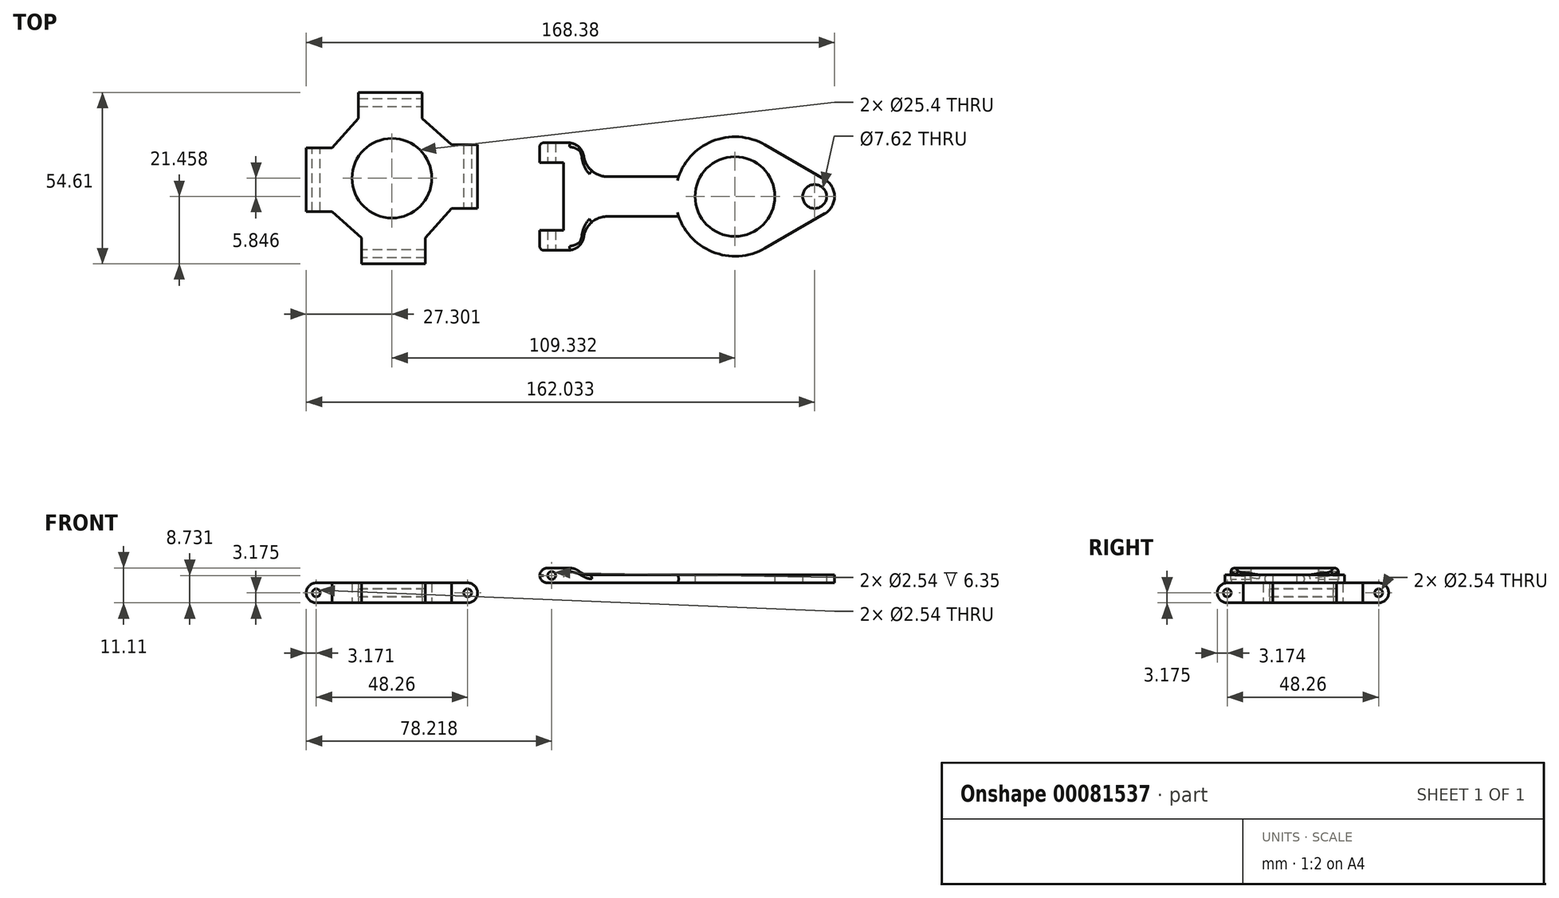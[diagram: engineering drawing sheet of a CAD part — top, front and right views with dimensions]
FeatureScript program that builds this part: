
annotation { "Feature Type Name" : "Feature", "Feature Type Description" : "" }
export const myFeature = defineFeature(function(context is Context, id is Id, definition is map)
    precondition{}
    {
        {
            var Q0;
            Q0=qCreatedBy(makeId("Top.planeOp"),FACE);
            var sketch = newSketch(context, id + "F0", { "sketchPlane" : qUnion([Q0])});
            skLineSegment(sketch, "E0.bottom", {"start": v(2.73, 19.55) * mm, "end": v(-35.37, 19.55) * mm});
            skLineSegment(sketch, "E0.top", {"start": v(2.73, -18.55) * mm, "end": v(-35.37, -18.55) * mm});
            skLineSegment(sketch, "E0.left", {"start": v(2.73, 19.55) * mm, "end": v(2.73, -18.55) * mm});
            skLineSegment(sketch, "E0.right", {"start": v(-35.37, 19.55) * mm, "end": v(-35.37, -18.55) * mm});
            skPoint(sketch, "E0.middle", {"position": v(-16.32, 0.5) * mm});
            skCircle(sketch, "E1", {"center": v(-16.32, 0.5) * mm, "radius": 12.7 * mm});
            skSolve(sketch);
        }
        {
            var Q0;
            Q0 = qSketchRegion(id + "F0", true);
            extrude(context, id + "F1", {"entities" : qUnion([Q0]), "depth" : 6.35 * mm});
        }
        {
            var Q0;
            Q0=qCreatedBy(makeId("Front.planeOp"),FACE);
            var sketch = newSketch(context, id + "F2", { "sketchPlane" : qUnion([Q0])});
            skCircle(sketch, "E2", {"center": v(-40.45, 3.17) * mm, "radius": 3.18 * mm});
            skCircle(sketch, "E3", {"center": v(-40.45, 3.17) * mm, "radius": 1.27 * mm});
            skLineSegment(sketch, "E4", {"start": v(-40.45, 6.35) * mm, "end": v(-35.37, 6.35) * mm});
            skLineSegment(sketch, "E5", {"start": v(-35.37, 6.35) * mm, "end": v(-35.37, 0) * mm});
            skLineSegment(sketch, "E6", {"start": v(-35.37, 0) * mm, "end": v(-40.45, 0) * mm});
            skSolve(sketch);
        }
        {
            var Q0;
            Q0 = qSketchRegion(id + "F2", true);
            extrude(context, id + "F3", {"entities" : qUnion([Q0]), "operationType" : NewBodyOperationType.ADD, "depth" : 10.16 * mm, "hasSecondDirection" : true, "secondDirectionOppositeDirection" : true, "secondDirectionDepth" : 10.16 * mm});
        }
        {
            var Q0;
            Q0=makeQuery(id+"F1.opExtrude","SWEPT_BODY",BODY,{"disambiguationData":[OSD([sQuery(id+"F0.wireOp",EDGE,"E0.bottom"),sQuery(id+"F0.wireOp",EDGE,"E0.top"),sQuery(id+"F0.wireOp",EDGE,"E0.left"),sQuery(id+"F0.wireOp",EDGE,"E0.right"),sQuery(id+"F0.wireOp",EDGE,"E1")])]});
            var Q1;
            Q1=makeQuery(id+"F1.opExtrude","CAP_EDGE",EDGE,{"disambiguationData":[OSD([sQuery(id+"F0.wireOp",EDGE,"E1")])],"isStart":false});
            circularPattern(context, id + "F4", {"operationType" : NewBodyOperationType.ADD, "entities" : qUnion([Q0]), "axis" : qUnion([Q1]), "angle" : 90 * degree, "instanceCount" : 4});
        }
        {
            var Q0;
            {var subQ0=makeQuery(id+"F3.boolean.opBoolean","MERGE",FACE,{"derivedFrom":[makeQuery(id+"F1.opExtrude","CAP_FACE",FACE,{"disambiguationData":[OSD([sQuery(id+"F0.wireOp",EDGE,"E0.bottom"),sQuery(id+"F0.wireOp",EDGE,"E0.top"),sQuery(id+"F0.wireOp",EDGE,"E0.left"),sQuery(id+"F0.wireOp",EDGE,"E0.right"),sQuery(id+"F0.wireOp",EDGE,"E1")])],"isStart":false}),makeQuery(id+"F3.opExtrude","SWEPT_FACE",FACE,{"disambiguationData":[OSD([sQuery(id+"F2.wireOp",EDGE,"E4")])]})]});Q0=makeQuery(id+"F4.boolean.opBoolean","MERGE",FACE,{"derivedFrom":[subQ0,makeQuery(id+"F4.opPattern","COPY",FACE,{"derivedFrom":subQ0,"instanceName":"1"}),makeQuery(id+"F4.opPattern","COPY",FACE,{"derivedFrom":subQ0,"instanceName":"2"}),makeQuery(id+"F4.opPattern","COPY",FACE,{"derivedFrom":subQ0,"instanceName":"3"})]});}
            var sketch = newSketch(context, id + "F5", { "sketchPlane" : qUnion([Q0])});
            skLineSegment(sketch, "E7", {"start": v(-26.98, 19.55) * mm, "end": v(-35.37, 10.16) * mm});
            skLineSegment(sketch, "E8", {"start": v(-35.37, 10.16) * mm, "end": v(-40.75, 19.55) * mm});
            skLineSegment(sketch, "E9", {"start": v(-40.75, 19.55) * mm, "end": v(-26.98, 19.55) * mm});
            skLineSegment(sketch, "E10", {"start": v(-6.66, 19.55) * mm, "end": v(2.73, 11.17) * mm});
            skLineSegment(sketch, "E11", {"start": v(2.73, 11.17) * mm, "end": v(6.16, 21.92) * mm});
            skLineSegment(sketch, "E12", {"start": v(6.16, 21.92) * mm, "end": v(-6.66, 19.55) * mm});
            skLineSegment(sketch, "E13", {"start": v(-35.37, -10.16) * mm, "end": v(-25.98, -18.55) * mm});
            skLineSegment(sketch, "E14", {"start": v(-25.98, -18.55) * mm, "end": v(-39.65, -26.32) * mm});
            skLineSegment(sketch, "E15", {"start": v(-39.65, -26.32) * mm, "end": v(-35.37, -10.16) * mm});
            skLineSegment(sketch, "E16", {"start": v(-5.66, -18.55) * mm, "end": v(10.18, -22.29) * mm});
            skLineSegment(sketch, "E17", {"start": v(10.18, -22.29) * mm, "end": v(2.73, -9.15) * mm});
            skLineSegment(sketch, "E18", {"start": v(2.73, -9.15) * mm, "end": v(-5.66, -18.55) * mm});
            skSolve(sketch);
        }
        {
            var Q0;
            Q0 = qSketchRegion(id + "F5", true);
            extrude(context, id + "F6", {"entities" : qUnion([Q0]), "operationType" : NewBodyOperationType.REMOVE, "endBound" : BoundingType.THROUGH_ALL, "oppositeDirection" : true, "depth" : 25.4 * mm});
        }
        {
            var Q0;
            {var subQ0=makeQuery(id+"F3.boolean.opBoolean","MERGE",FACE,{"derivedFrom":[makeQuery(id+"F1.opExtrude","CAP_FACE",FACE,{"disambiguationData":[OSD([sQuery(id+"F0.wireOp",EDGE,"E0.bottom"),sQuery(id+"F0.wireOp",EDGE,"E0.top"),sQuery(id+"F0.wireOp",EDGE,"E0.left"),sQuery(id+"F0.wireOp",EDGE,"E0.right"),sQuery(id+"F0.wireOp",EDGE,"E1")])],"isStart":false}),makeQuery(id+"F3.opExtrude","SWEPT_FACE",FACE,{"disambiguationData":[OSD([sQuery(id+"F2.wireOp",EDGE,"E4")])]})]});Q0=makeQuery(id+"F4.boolean.opBoolean","MERGE",FACE,{"derivedFrom":[subQ0,makeQuery(id+"F4.opPattern","COPY",FACE,{"derivedFrom":subQ0,"instanceName":"1"}),makeQuery(id+"F4.opPattern","COPY",FACE,{"derivedFrom":subQ0,"instanceName":"2"}),makeQuery(id+"F4.opPattern","COPY",FACE,{"derivedFrom":subQ0,"instanceName":"3"})]});}
            var sketch = newSketch(context, id + "F7", { "sketchPlane" : qUnion([Q0])});
            skLineSegment(sketch, "E19", {"start": v(30.78, 11.8) * mm, "end": v(30.78, 5.45) * mm});
            skLineSegment(sketch, "E20", {"start": v(30.78, 5.45) * mm, "end": v(38.4, 5.45) * mm});
            skLineSegment(sketch, "E21", {"start": v(38.4, 5.45) * mm, "end": v(38.4, -16.14) * mm});
            skLineSegment(sketch, "E22", {"start": v(38.4, -16.14) * mm, "end": v(30.78, -16.14) * mm});
            skLineSegment(sketch, "E23", {"start": v(30.78, -16.14) * mm, "end": v(30.78, -22.49) * mm});
            skLineSegment(sketch, "E24", {"start": v(30.78, -22.49) * mm, "end": v(44.75, -22.49) * mm});
            skLineSegment(sketch, "E25", {"start": v(44.75, -22.49) * mm, "end": v(44.75, -11.7) * mm});
            skLineSegment(sketch, "E26", {"start": v(44.75, -11.7) * mm, "end": v(67.61, -11.7) * mm});
            skLineSegment(sketch, "E27", {"start": v(67.61, 1) * mm, "end": v(44.75, 1) * mm});
            skLineSegment(sketch, "E28", {"start": v(44.75, 1) * mm, "end": v(44.75, 11.8) * mm});
            skLineSegment(sketch, "E29", {"start": v(44.75, 11.8) * mm, "end": v(30.78, 11.8) * mm});
            skCircle(sketch, "E30", {"center": v(93.01, -5.34) * mm, "radius": 19.05 * mm});
            skCircle(sketch, "E31", {"center": v(93.01, -5.34) * mm, "radius": 12.7 * mm});
            skLineSegment(sketch, "E32", {"start": v(67.61, 1) * mm, "end": v(75.05, 1) * mm});
            skLineSegment(sketch, "E33", {"start": v(75.05, 1) * mm, "end": v(75.05, -11.7) * mm});
            skLineSegment(sketch, "E34", {"start": v(75.05, -11.7) * mm, "end": v(67.61, -11.7) * mm});
            skCircle(sketch, "E35", {"center": v(118.41, -5.34) * mm, "radius": 6.35 * mm});
            skLineSegment(sketch, "E36", {"start": v(102.54, -21.84) * mm, "end": v(121.59, -10.84) * mm});
            skLineSegment(sketch, "E37", {"start": v(121.59, -10.84) * mm, "end": v(121.59, 0.16) * mm});
            skLineSegment(sketch, "E38", {"start": v(121.59, 0.16) * mm, "end": v(102.54, 11.16) * mm});
            skCircle(sketch, "E39", {"center": v(118.41, -5.34) * mm, "radius": 3.81 * mm});
            skSolve(sketch);
        }
        {
            var Q0;
            Q0=makeQuery(id+"F7.imprint","IMPRINT",FACE,{"disambiguationData":[TD([[makeQuery(id+"F7.imprint","IMPRINT",EDGE,{"derivedFrom":sQuery(id+"F7.wireOp",EDGE,"E19")}),1.0]])]});
            var Q1;
            {var subQ1=sQuery(id+"F7.wireOp",EDGE,"XL47u7Ki-qIGk-DITZ-stqT-tPDxZNCZAFx5");Q1=makeQuery(id+"F7.imprint","IMPRINT",FACE,{"disambiguationData":[TD([[makeQuery(id+"F7.imprint","IMPRINT",EDGE,{"derivedFrom":subQ1}),1.0]])]});}
            var Q2;
            Q2=makeQuery(id+"F7.imprint","IMPRINT",FACE,{"disambiguationData":[TD([[makeQuery(id+"F7.imprint","IMPRINT",EDGE,{"derivedFrom":sQuery(id+"F7.wireOp",EDGE,"E31")}),-1.0]])]});
            var Q3;
            {var subQ0=sQuery(id+"F7.wireOp",EDGE,"E33");Q3=makeQuery(id+"F7.imprint","IMPRINT",FACE,{"disambiguationData":[TD([[makeQuery(id+"F7.imprint","IMPRINT",EDGE,{"derivedFrom":subQ0}),-1.0]])]});}
            var Q4;
            {var subQ0=sQuery(id+"F7.wireOp",EDGE,"E36");Q4=makeQuery(id+"F7.imprint","IMPRINT",FACE,{"disambiguationData":[TD([[makeQuery(id+"F7.imprint","IMPRINT",EDGE,{"derivedFrom":subQ0}),1.0]])]});}
            var Q5;
            {var subQ0=sQuery(id+"F7.wireOp",EDGE,"E38");Q5=makeQuery(id+"F7.imprint","IMPRINT",FACE,{"disambiguationData":[TD([[makeQuery(id+"F7.imprint","IMPRINT",EDGE,{"derivedFrom":subQ0}),1.0]])]});}
            var Q6;
            {var subQ0=sQuery(id+"F7.wireOp",EDGE,"E37");var subQ3=sQuery(id+"F7.wireOp",EDGE,"E39");var subQ6=makeQuery(id+"F7.imprint","INTERSECT",VERTEX,{"disambiguationData":[OD(0.0)],"derivedFrom":[subQ0,subQ3]});Q6=makeQuery(id+"F7.imprint","IMPRINT",FACE,{"disambiguationData":[TD([[makeQuery(id+"F7.imprint","IMPRINT",EDGE,{"disambiguationData":[TD([[subQ6,1.0]])],"derivedFrom":subQ3}),-1.0]])]});}
            var Q7;
            {var subQ0=sQuery(id+"F7.wireOp",EDGE,"E37");var subQ4=sQuery(id+"F7.wireOp",EDGE,"E39");var subQ5=makeQuery(id+"F7.imprint","INTERSECT",VERTEX,{"disambiguationData":[OD(0.0)],"derivedFrom":[subQ0,subQ4]});Q7=makeQuery(id+"F7.imprint","IMPRINT",FACE,{"disambiguationData":[TD([[makeQuery(id+"F7.imprint","IMPRINT",EDGE,{"disambiguationData":[TD([[subQ5,-1.0]])],"derivedFrom":subQ4}),-1.0]])]});}
            extrude(context, id + "F8", {"entities" : qUnion([Q0, Q1, Q2, Q3, Q4, Q5, Q6, Q7]), "depth" : 4.76 * mm});
        }
        {
            var Q0;
            Q0=makeQuery(id+"F8.opExtrude","SWEPT_EDGE",EDGE,{"disambiguationData":[OSD([sQuery(id+"F7.wireOp",EDGE,"Hxhbranr-2qHg-c5iI-VbZw-sH5m9WmZGcHk"),sQuery(id+"F7.wireOp",EDGE,"OMfF5kUA-ekjO-Me9f-fNz4-odrc9yjyQ8z9")])]});
            var Q1;
            Q1=makeQuery(id+"F8.opExtrude","SWEPT_EDGE",EDGE,{"disambiguationData":[OSD([sQuery(id+"F7.wireOp",EDGE,"OMfF5kUA-ekjO-Me9f-fNz4-odrc9yjyQ8z9"),sQuery(id+"F7.wireOp",EDGE,"XL47u7Ki-qIGk-DITZ-stqT-tPDxZNCZAFx5"),sQuery(id+"F7.wireOp",EDGE,"nL18PZB6-yZRc-0n0b-8FF0-d2ZYOT2c4TUV")])]});
            var Q2;
            Q2=makeQuery(id+"F8.opExtrude","SWEPT_EDGE",EDGE,{"disambiguationData":[OSD([sQuery(id+"F7.wireOp",EDGE,"XL47u7Ki-qIGk-DITZ-stqT-tPDxZNCZAFx5"),sQuery(id+"F7.wireOp",EDGE,"NSSHPLKI-I9TS-wmt4-1eJO-JCgIBDZXPaOh")])]});
            var Q3;
            Q3=makeQuery(id+"F8.opExtrude","SWEPT_EDGE",EDGE,{"disambiguationData":[OSD([sQuery(id+"F7.wireOp",EDGE,"NSSHPLKI-I9TS-wmt4-1eJO-JCgIBDZXPaOh"),sQuery(id+"F7.wireOp",EDGE,"JB2rgTsf-Nh2k-UzIR-AXvc-0LokfaTkBtxn"),sQuery(id+"F7.wireOp",EDGE,"nL18PZB6-yZRc-0n0b-8FF0-d2ZYOT2c4TUV")])]});
            var Q4;
            Q4=makeQuery(id+"F8.opExtrude","SWEPT_EDGE",EDGE,{"disambiguationData":[OSD([sQuery(id+"F7.wireOp",EDGE,"JB2rgTsf-Nh2k-UzIR-AXvc-0LokfaTkBtxn"),sQuery(id+"F7.wireOp",EDGE,"E27")])]});
            var Q5;
            Q5=makeQuery(id+"F8.opExtrude","SWEPT_EDGE",EDGE,{"disambiguationData":[OSD([sQuery(id+"F7.wireOp",EDGE,"E26"),sQuery(id+"F7.wireOp",EDGE,"Hxhbranr-2qHg-c5iI-VbZw-sH5m9WmZGcHk")])]});
            fillet(context, id + "F9", {"entities" : qUnion([Q0, Q1, Q2, Q3, Q4, Q5]), "radius" : 7.62 * mm, "tangentPropagation" : true, "allowEdgeOverflow" : false});
        }
        {
            var Q0;
            Q0=makeQuery(id+"F8.opExtrude","SWEPT_EDGE",EDGE,{"disambiguationData":[OSD([sQuery(id+"F7.wireOp",EDGE,"E24"),sQuery(id+"F7.wireOp",EDGE,"E25")])]});
            var Q1;
            Q1=makeQuery(id+"F8.opExtrude","SWEPT_EDGE",EDGE,{"disambiguationData":[OSD([sQuery(id+"F7.wireOp",EDGE,"E27"),sQuery(id+"F7.wireOp",EDGE,"E28")])]});
            var Q2;
            Q2=makeQuery(id+"F8.opExtrude","SWEPT_EDGE",EDGE,{"disambiguationData":[OSD([sQuery(id+"F7.wireOp",EDGE,"E28"),sQuery(id+"F7.wireOp",EDGE,"E29")])]});
            var Q3;
            Q3=makeQuery(id+"F8.opExtrude","SWEPT_EDGE",EDGE,{"disambiguationData":[OSD([sQuery(id+"F7.wireOp",EDGE,"E25"),sQuery(id+"F7.wireOp",EDGE,"E26")])]});
            fillet(context, id + "F10", {"entities" : qUnion([Q0, Q1, Q2, Q3]), "radius" : 5.08 * mm, "tangentPropagation" : true, "allowEdgeOverflow" : false});
        }
        {
            var Q0;
            Q0=makeQuery(id+"F8.opExtrude","CAP_EDGE",EDGE,{"disambiguationData":[OSD([sQuery(id+"F7.wireOp",EDGE,"E19")])],"isStart":false});
            var Q1;
            Q1=makeQuery(id+"F8.opExtrude","CAP_EDGE",EDGE,{"disambiguationData":[OSD([sQuery(id+"F7.wireOp",EDGE,"E19")])],"isStart":true});
            var Q2;
            Q2=makeQuery(id+"F8.opExtrude","CAP_EDGE",EDGE,{"disambiguationData":[OSD([sQuery(id+"F7.wireOp",EDGE,"E23")])],"isStart":false});
            var Q3;
            Q3=makeQuery(id+"F8.opExtrude","CAP_EDGE",EDGE,{"disambiguationData":[OSD([sQuery(id+"F7.wireOp",EDGE,"E23")])],"isStart":true});
            fillet(context, id + "F11", {"entities" : qUnion([Q0, Q1, Q2, Q3]), "radius" : 2.54 * mm, "tangentPropagation" : true, "allowEdgeOverflow" : false});
        }
        {
            var Q0;
            Q0=makeQuery(id+"F8.opExtrude","SWEPT_FACE",FACE,{"disambiguationData":[OSD([sQuery(id+"F7.wireOp",EDGE,"E24")])]});
            var sketch = newSketch(context, id + "F12", { "sketchPlane" : qUnion([Q0])});
            skLineSegment(sketch, "E40", {"start": v(30.79, 8.73) * mm, "end": v(34.6, 8.73) * mm});
            skCircle(sketch, "E41", {"center": v(34.6, 8.73) * mm, "radius": 1.27 * mm});
            skSolve(sketch);
        }
        {
            var Q0;
            Q0 = qSketchRegion(id + "F12", true);
            extrude(context, id + "F13", {"entities" : qUnion([Q0]), "operationType" : NewBodyOperationType.REMOVE, "endBound" : BoundingType.THROUGH_ALL, "oppositeDirection" : true, "depth" : 25.4 * mm});
        }
        {
            var Q0;
            Q0=makeQuery(id+"F8.opExtrude","CAP_FACE",FACE,{"disambiguationData":[OSD([sQuery(id+"F7.wireOp",EDGE,"E19"),sQuery(id+"F7.wireOp",EDGE,"E20"),sQuery(id+"F7.wireOp",EDGE,"E21"),sQuery(id+"F7.wireOp",EDGE,"E22"),sQuery(id+"F7.wireOp",EDGE,"E23"),sQuery(id+"F7.wireOp",EDGE,"E24"),sQuery(id+"F7.wireOp",EDGE,"E25"),sQuery(id+"F7.wireOp",EDGE,"E26"),sQuery(id+"F7.wireOp",EDGE,"E27"),sQuery(id+"F7.wireOp",EDGE,"E28"),sQuery(id+"F7.wireOp",EDGE,"E29"),sQuery(id+"F7.wireOp",EDGE,"E30"),sQuery(id+"F7.wireOp",EDGE,"E31"),sQuery(id+"F7.wireOp",EDGE,"E32"),sQuery(id+"F7.wireOp",EDGE,"E34")])],"isStart":false});
            var sketch = newSketch(context, id + "F14", { "sketchPlane" : qUnion([Q0])});
            skLineSegment(sketch, "E42.bottom", {"start": v(42.4, 19.2) * mm, "end": v(147.31, 19.2) * mm});
            skLineSegment(sketch, "E42.top", {"start": v(42.4, -31.49) * mm, "end": v(147.31, -31.49) * mm});
            skLineSegment(sketch, "E42.left", {"start": v(42.4, 19.2) * mm, "end": v(42.4, -31.49) * mm});
            skLineSegment(sketch, "E42.right", {"start": v(147.31, 19.2) * mm, "end": v(147.31, -31.49) * mm});
            skSolve(sketch);
        }
        {
            var Q0;
            Q0 = qSketchRegion(id + "F14", true);
            extrude(context, id + "F15", {"entities" : qUnion([Q0]), "operationType" : NewBodyOperationType.REMOVE, "oppositeDirection" : true, "depth" : 2.22 * mm});
        }
        {
            var Q0;
            Q0=makeQuery(id+"F15.boolean.opBoolean","COPY",EDGE,{"derivedFrom":makeQuery(id+"F15.opExtrude","CAP_EDGE",EDGE,{"disambiguationData":[OSD([sQuery(id+"F14.wireOp",EDGE,"E42.left")])],"isStart":false})});
            fillet(context, id + "F16", {"entities" : qUnion([Q0]), "radius" : 5.08 * mm, "tangentPropagation" : true, "allowEdgeOverflow" : false});
        }
        {
            var Q0;
            Q0=makeQuery(id+"F16.opFillet","BLEND_EDGE",EDGE,{"blendedFrom":[makeQuery(id+"F15.boolean.opBoolean","COPY",EDGE,{"derivedFrom":makeQuery(id+"F15.opExtrude","CAP_EDGE",EDGE,{"disambiguationData":[OSD([sQuery(id+"F14.wireOp",EDGE,"E42.left")])],"isStart":false})}),makeQuery(id+"F8.opExtrude","CAP_FACE",FACE,{"disambiguationData":[OSD([sQuery(id+"F7.wireOp",EDGE,"E19"),sQuery(id+"F7.wireOp",EDGE,"E20"),sQuery(id+"F7.wireOp",EDGE,"E21"),sQuery(id+"F7.wireOp",EDGE,"E22"),sQuery(id+"F7.wireOp",EDGE,"E23"),sQuery(id+"F7.wireOp",EDGE,"E24"),sQuery(id+"F7.wireOp",EDGE,"E25"),sQuery(id+"F7.wireOp",EDGE,"E26"),sQuery(id+"F7.wireOp",EDGE,"E27"),sQuery(id+"F7.wireOp",EDGE,"E28"),sQuery(id+"F7.wireOp",EDGE,"E29"),sQuery(id+"F7.wireOp",EDGE,"E30"),sQuery(id+"F7.wireOp",EDGE,"E31"),sQuery(id+"F7.wireOp",EDGE,"E32"),sQuery(id+"F7.wireOp",EDGE,"E34")])],"isStart":false})],"blendedInto":[makeQuery(id+"F8.opExtrude","CAP_FACE",FACE,{"disambiguationData":[OSD([sQuery(id+"F7.wireOp",EDGE,"E19"),sQuery(id+"F7.wireOp",EDGE,"E20"),sQuery(id+"F7.wireOp",EDGE,"E21"),sQuery(id+"F7.wireOp",EDGE,"E22"),sQuery(id+"F7.wireOp",EDGE,"E23"),sQuery(id+"F7.wireOp",EDGE,"E24"),sQuery(id+"F7.wireOp",EDGE,"E25"),sQuery(id+"F7.wireOp",EDGE,"E26"),sQuery(id+"F7.wireOp",EDGE,"E27"),sQuery(id+"F7.wireOp",EDGE,"E28"),sQuery(id+"F7.wireOp",EDGE,"E29"),sQuery(id+"F7.wireOp",EDGE,"E30"),sQuery(id+"F7.wireOp",EDGE,"E31"),sQuery(id+"F7.wireOp",EDGE,"E32"),sQuery(id+"F7.wireOp",EDGE,"E34")])],"isStart":false})]});
            fillet(context, id + "F17", {"entities" : qUnion([Q0]), "radius" : 5.08 * mm, "tangentPropagation" : true, "allowEdgeOverflow" : false});
        }
        {
            var Q0;
            Q0=makeQuery(id+"F15.boolean.opBoolean","INTERSECT",EDGE,{"derivedFrom":[makeQuery(id+"F8.opExtrude","SWEPT_FACE",FACE,{"disambiguationData":[OSD([sQuery(id+"F7.wireOp",EDGE,"E26"),sQuery(id+"F7.wireOp",EDGE,"E34")])]}),makeQuery(id+"F15.opExtrude","CAP_FACE",FACE,{"disambiguationData":[OSD([sQuery(id+"F14.wireOp",EDGE,"E42.bottom"),sQuery(id+"F14.wireOp",EDGE,"E42.top"),sQuery(id+"F14.wireOp",EDGE,"E42.left"),sQuery(id+"F14.wireOp",EDGE,"E42.right")])],"isStart":false})]});
            var Q1;
            Q1=makeQuery(id+"F8.opExtrude","CAP_EDGE",EDGE,{"disambiguationData":[OSD([sQuery(id+"F7.wireOp",EDGE,"E26"),sQuery(id+"F7.wireOp",EDGE,"E34")])],"isStart":true});
            var Q2;
            Q2=makeQuery(id+"F15.boolean.opBoolean","INTERSECT",EDGE,{"derivedFrom":[makeQuery(id+"F8.opExtrude","SWEPT_FACE",FACE,{"disambiguationData":[OSD([sQuery(id+"F7.wireOp",EDGE,"E27"),sQuery(id+"F7.wireOp",EDGE,"E32")])]}),makeQuery(id+"F15.opExtrude","CAP_FACE",FACE,{"disambiguationData":[OSD([sQuery(id+"F14.wireOp",EDGE,"E42.bottom"),sQuery(id+"F14.wireOp",EDGE,"E42.top"),sQuery(id+"F14.wireOp",EDGE,"E42.left"),sQuery(id+"F14.wireOp",EDGE,"E42.right")])],"isStart":false})]});
            var Q3;
            Q3=makeQuery(id+"F8.opExtrude","CAP_EDGE",EDGE,{"disambiguationData":[OSD([sQuery(id+"F7.wireOp",EDGE,"E27"),sQuery(id+"F7.wireOp",EDGE,"E32")])],"isStart":true});
            fillet(context, id + "F18", {"entities" : qUnion([Q0, Q1, Q2, Q3]), "radius" : 1.27 * mm, "tangentPropagation" : true, "allowEdgeOverflow" : false});
        }
    });
